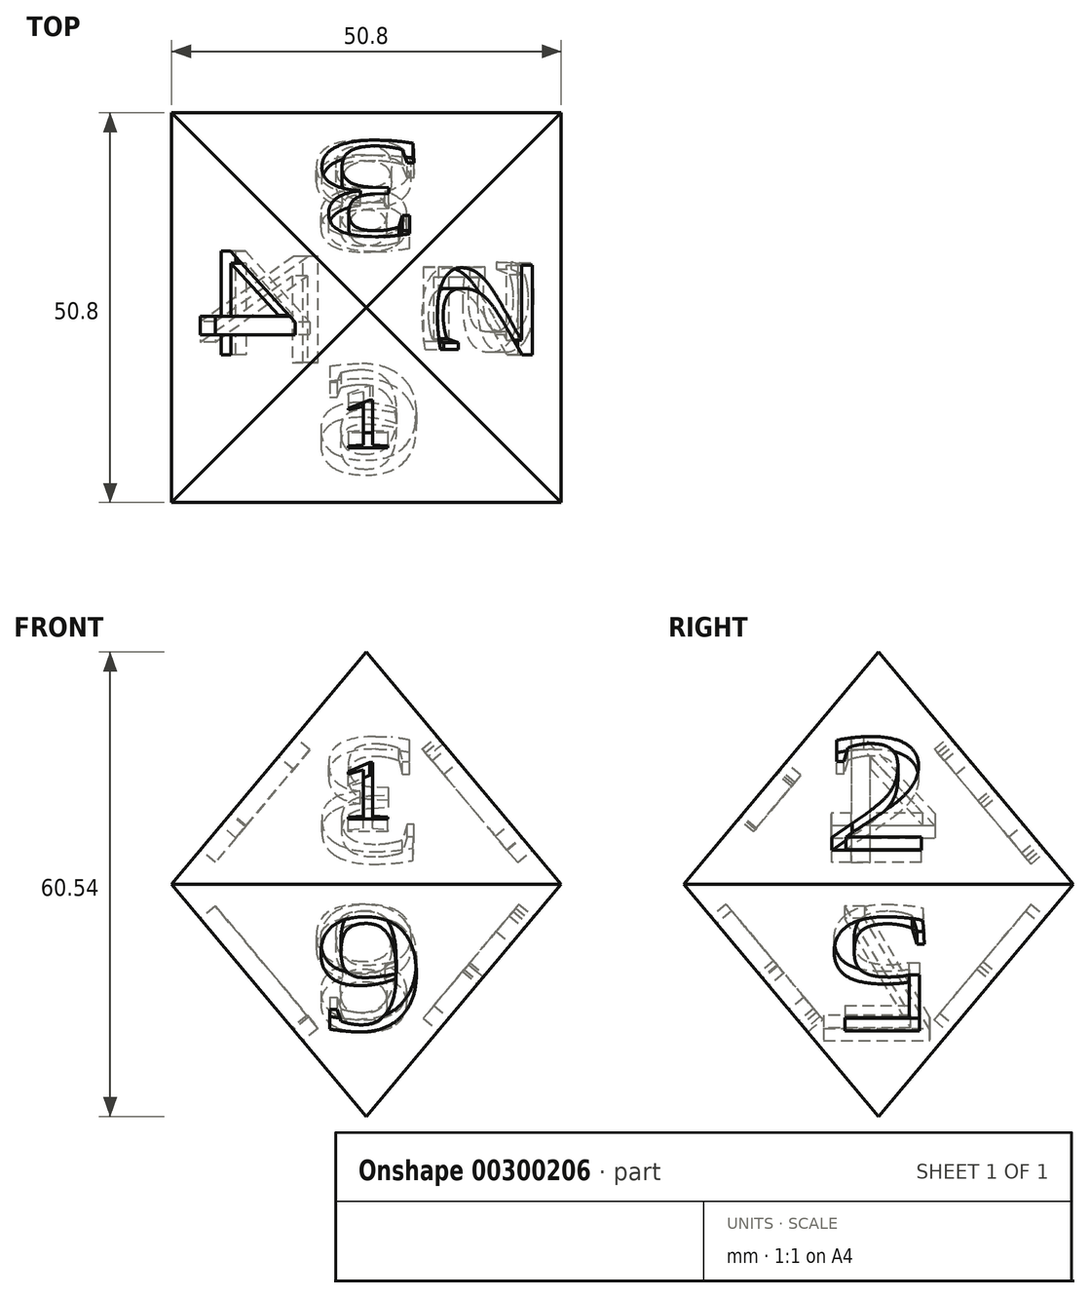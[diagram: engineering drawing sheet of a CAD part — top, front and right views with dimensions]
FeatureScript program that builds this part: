
annotation { "Feature Type Name" : "Feature", "Feature Type Description" : "" }
export const myFeature = defineFeature(function(context is Context, id is Id, definition is map)
    precondition{}
    {
        {
            var Q0;
            Q0=qCreatedBy(makeId("Top.planeOp"),FACE);
            var sketch = newSketch(context, id + "F0", { "sketchPlane" : qUnion([Q0])});
            skLineSegment(sketch, "E0.bottom", {"start": v(25.4, -25.4) * mm, "end": v(-25.4, -25.4) * mm});
            skLineSegment(sketch, "E0.top", {"start": v(25.4, 25.4) * mm, "end": v(-25.4, 25.4) * mm});
            skLineSegment(sketch, "E0.left", {"start": v(25.4, -25.4) * mm, "end": v(25.4, 25.4) * mm});
            skLineSegment(sketch, "E0.right", {"start": v(-25.4, -25.4) * mm, "end": v(-25.4, 25.4) * mm});
            skPoint(sketch, "E0.middle", {"position": v(0, 0) * mm});
            skSolve(sketch);
        }
        {
            var Q0;
            Q0 = qSketchRegion(id + "F0", true);
            extrude(context, id + "F1", {"entities" : qUnion([Q0]), "depth" : 38.1 * mm, "hasDraft" : true, "draftAngle" : 40 * degree, "draftPullDirection" : true});
        }
        {
            var Q0;
            Q0 = qSketchRegion(id + "F0", true);
            extrude(context, id + "F2", {"entities" : qUnion([Q0]), "operationType" : NewBodyOperationType.ADD, "oppositeDirection" : true, "depth" : 38.1 * mm, "hasDraft" : true, "draftAngle" : 40 * degree, "draftPullDirection" : true});
        }
        {
            var Q0;
            Q0=makeQuery(id+"F1.opExtrude","SWEPT_FACE",FACE,{"disambiguationData":[OSD([sQuery(id+"F0.wireOp",EDGE,"E0.bottom")])]});
            var sketch = newSketch(context, id + "F3", { "sketchPlane" : qUnion([Q0])});
            skText(sketch, "E1", { "text": "1", "fontName": "Tinos-Regular.ttf"});
            const initialGuessF3  = {"E1": [-0.00367, -0.00526, 1, 0, 0.01052]};
            skSetInitialGuess(sketch, initialGuessF3);
            skSolve(sketch);
        }
        {
            var Q0;
            Q0 = qSketchRegion(id + "F3", true);
            extrude(context, id + "F4", {"entities" : qUnion([Q0]), "operationType" : NewBodyOperationType.REMOVE, "oppositeDirection" : true, "depth" : 2.54 * mm});
        }
        {
            var Q0;
            Q0=makeQuery(id+"F2.opExtrude","SWEPT_FACE",FACE,{"disambiguationData":[OSD([sQuery(id+"F0.wireOp",EDGE,"E0.top")])]});
            var sketch = newSketch(context, id + "F5", { "sketchPlane" : qUnion([Q0])});
            skText(sketch, "E2", { "text": "8", "fontName": "Tinos-Regular.ttf"});
            const initialGuessF5  = {"E2": [0.00764, 0.01049, -1, 0, 0.02098]};
            skSetInitialGuess(sketch, initialGuessF5);
            skSolve(sketch);
        }
        {
            var Q0;
            Q0 = qSketchRegion(id + "F5", true);
            extrude(context, id + "F6", {"entities" : qUnion([Q0]), "operationType" : NewBodyOperationType.REMOVE, "oppositeDirection" : true, "depth" : 2.54 * mm});
        }
        {
            var Q0;
            Q0=makeQuery(id+"F1.opExtrude","SWEPT_FACE",FACE,{"disambiguationData":[OSD([sQuery(id+"F0.wireOp",EDGE,"E0.left")])]});
            var sketch = newSketch(context, id + "F7", { "sketchPlane" : qUnion([Q0])});
            skText(sketch, "E3", { "text": "2", "fontName": "Tinos-Regular.ttf"});
            const initialGuessF7  = {"E3": [-0.0074, -0.01049, 1, 0, 0.02098]};
            skSetInitialGuess(sketch, initialGuessF7);
            skSolve(sketch);
        }
        {
            var Q0;
            Q0 = qSketchRegion(id + "F7", true);
            extrude(context, id + "F8", {"entities" : qUnion([Q0]), "operationType" : NewBodyOperationType.REMOVE, "oppositeDirection" : true, "depth" : 2.54 * mm});
        }
        {
            var Q0;
            Q0=makeQuery(id+"F2.opExtrude","SWEPT_FACE",FACE,{"disambiguationData":[OSD([sQuery(id+"F0.wireOp",EDGE,"E0.right")])]});
            var sketch = newSketch(context, id + "F9", { "sketchPlane" : qUnion([Q0])});
            skText(sketch, "E4", { "text": "7", "fontName": "OpenSans-Regular.ttf"});
            const initialGuessF9  = {"E4": [0.00853, 0.01049, -1, 0, 0.02098]};
            skSetInitialGuess(sketch, initialGuessF9);
            skSolve(sketch);
        }
        {
            var Q0;
            Q0 = qSketchRegion(id + "F9", true);
            extrude(context, id + "F10", {"entities" : qUnion([Q0]), "operationType" : NewBodyOperationType.REMOVE, "oppositeDirection" : true, "depth" : 2.54 * mm});
        }
        {
            var Q0;
            Q0=makeQuery(id+"F2.opExtrude","SWEPT_FACE",FACE,{"disambiguationData":[OSD([sQuery(id+"F0.wireOp",EDGE,"E0.bottom")])]});
            var sketch = newSketch(context, id + "F11", { "sketchPlane" : qUnion([Q0])});
            skText(sketch, "E5", { "text": "6", "fontName": "Tinos-Regular.ttf"});
            const initialGuessF11  = {"E5": [0.00776, 0.01049, -1, 0, 0.02098]};
            skSetInitialGuess(sketch, initialGuessF11);
            skSolve(sketch);
        }
        {
            var Q0;
            Q0 = qSketchRegion(id + "F11", true);
            extrude(context, id + "F12", {"entities" : qUnion([Q0]), "operationType" : NewBodyOperationType.REMOVE, "oppositeDirection" : true, "depth" : 2.54 * mm});
        }
        {
            var Q0;
            Q0=makeQuery(id+"F1.opExtrude","SWEPT_FACE",FACE,{"disambiguationData":[OSD([sQuery(id+"F0.wireOp",EDGE,"E0.top")])]});
            var sketch = newSketch(context, id + "F13", { "sketchPlane" : qUnion([Q0])});
            skText(sketch, "E6", { "text": "3", "fontName": "Tinos-Regular.ttf"});
            const initialGuessF13  = {"E6": [-0.00763, -0.01049, 1, 0, 0.02098]};
            skSetInitialGuess(sketch, initialGuessF13);
            skSolve(sketch);
        }
        {
            var Q0;
            Q0 = qSketchRegion(id + "F13", true);
            extrude(context, id + "F14", {"entities" : qUnion([Q0]), "operationType" : NewBodyOperationType.REMOVE, "oppositeDirection" : true, "depth" : 2.54 * mm});
        }
        {
            var Q0;
            Q0=makeQuery(id+"F2.opExtrude","SWEPT_FACE",FACE,{"disambiguationData":[OSD([sQuery(id+"F0.wireOp",EDGE,"E0.left")])]});
            var sketch = newSketch(context, id + "F15", { "sketchPlane" : qUnion([Q0])});
            skText(sketch, "E7", { "text": "5", "fontName": "Tinos-Regular.ttf"});
            const initialGuessF15  = {"E7": [0.00763, 0.01049, -1, 0, 0.02098]};
            skSetInitialGuess(sketch, initialGuessF15);
            skSolve(sketch);
        }
        {
            var Q0;
            Q0 = qSketchRegion(id + "F15", true);
            extrude(context, id + "F16", {"entities" : qUnion([Q0]), "operationType" : NewBodyOperationType.REMOVE, "oppositeDirection" : true, "depth" : 2.54 * mm});
        }
        {
            var Q0;
            Q0=makeQuery(id+"F1.opExtrude","SWEPT_FACE",FACE,{"disambiguationData":[OSD([sQuery(id+"F0.wireOp",EDGE,"E0.right")])]});
            var sketch = newSketch(context, id + "F17", { "sketchPlane" : qUnion([Q0])});
            skText(sketch, "E8", { "text": "4", "fontName": "Tinos-Regular.ttf"});
            const initialGuessF17  = {"E8": [-0.00797, -0.01049, 1, 0, 0.02098]};
            skSetInitialGuess(sketch, initialGuessF17);
            skSolve(sketch);
        }
        {
            var Q0;
            Q0 = qSketchRegion(id + "F17", true);
            extrude(context, id + "F18", {"entities" : qUnion([Q0]), "operationType" : NewBodyOperationType.REMOVE, "oppositeDirection" : true, "depth" : 2.54 * mm});
        }
    });
